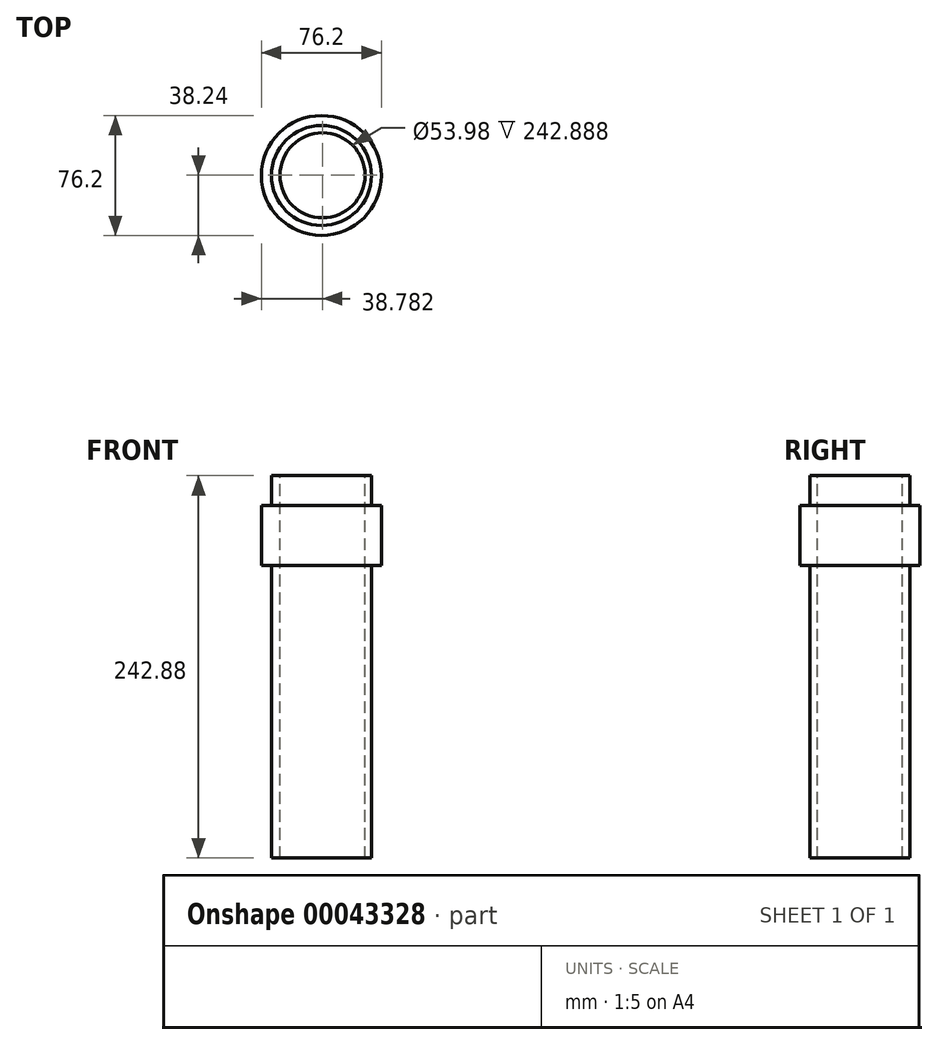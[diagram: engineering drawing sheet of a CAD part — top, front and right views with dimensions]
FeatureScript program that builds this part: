
annotation { "Feature Type Name" : "Feature", "Feature Type Description" : "" }
export const myFeature = defineFeature(function(context is Context, id is Id, definition is map)
    precondition{}
    {
        {
            var Q0;
            Q0=qCreatedBy(makeId("Front.planeOp"),FACE);
            var sketch = newSketch(context, id + "F0", { "sketchPlane" : qUnion([Q0])});
            skLineSegment(sketch, "E0.bottom", {"start": v(-31.75, 143.75) * mm, "end": v(0, 143.75) * mm});
            skLineSegment(sketch, "E0.top", {"start": v(-31.75, -99.13) * mm, "end": v(0, -99.13) * mm});
            skLineSegment(sketch, "E0.left", {"start": v(-31.75, 143.75) * mm, "end": v(-31.75, -99.13) * mm});
            skLineSegment(sketch, "E0.right", {"start": v(0, 143.75) * mm, "end": v(0, -99.13) * mm});
            skLineSegment(sketch, "E1.bottom", {"start": v(-38.1, 124.7) * mm, "end": v(-31.75, 124.7) * mm});
            skLineSegment(sketch, "E1.top", {"start": v(-38.1, 86.6) * mm, "end": v(-31.75, 86.6) * mm});
            skLineSegment(sketch, "E1.left", {"start": v(-38.1, 124.7) * mm, "end": v(-38.1, 86.6) * mm});
            skLineSegment(sketch, "E1.right", {"start": v(-31.75, 124.7) * mm, "end": v(-31.75, 86.6) * mm});
            skSolve(sketch);
        }
        {
            var Q0;
            Q0=makeQuery(id+"F0.imprint","IMPRINT",FACE,{"disambiguationData":[TD([[makeQuery(id+"F0.imprint","IMPRINT",EDGE,{"derivedFrom":sQuery(id+"F0.wireOp",EDGE,"E1.bottom")}),-1.0]])]});
            var Q1;
            {var subQ0=sQuery(id+"F0.wireOp",EDGE,"E0.bottom");Q1=makeQuery(id+"F0.imprint","IMPRINT",FACE,{"disambiguationData":[TD([[makeQuery(id+"F0.imprint","IMPRINT",EDGE,{"derivedFrom":subQ0}),-1.0]])]});}
            var Q2;
            Q2=sQuery(id+"F0.wireOp",EDGE,"E0.right");
            revolve(context, id + "F1", {"entities" : qUnion([Q0, Q1]), "axis" : qUnion([Q2]), "revolveType" : RevolveType.FULL});
        }
        {
            var Q0;
            Q0=qCreatedBy(makeId("Top.planeOp"),FACE);
            cPlane(context, id + "F2", {"entities" : qUnion([Q0]), "cplaneType" : CPlaneType.OFFSET, "offset" : 152.4 * mm, "width" : 152.4 * mm, "height" : 152.4 * mm});
        }
        {
            var Q0;
            Q0=qCreatedBy(id+"F2.planeOp",FACE);
            var sketch = newSketch(context, id + "F3", { "sketchPlane" : qUnion([Q0])});
            skCircle(sketch, "E2", {"center": v(0.68, 0.14) * mm, "radius": 26.99 * mm});
            skSolve(sketch);
        }
        {
            var Q0;
            Q0=makeQuery(id+"F3.imprint","IMPRINT",FACE,{"disambiguationData":[TD([[makeQuery(id+"F3.imprint","IMPRINT",EDGE,{"derivedFrom":sQuery(id+"F3.wireOp",EDGE,"E2")}),1.0]])]});
            var Q1;
            Q1=sQuery(id+"F3.wireOp",EDGE,"E2");
            extrude(context, id + "F4", {"entities" : qUnion([Q0]), "operationType" : NewBodyOperationType.REMOVE, "surfaceEntities" : qUnion([Q1]), "oppositeDirection" : true, "depth" : 381 * mm});
        }
    });
